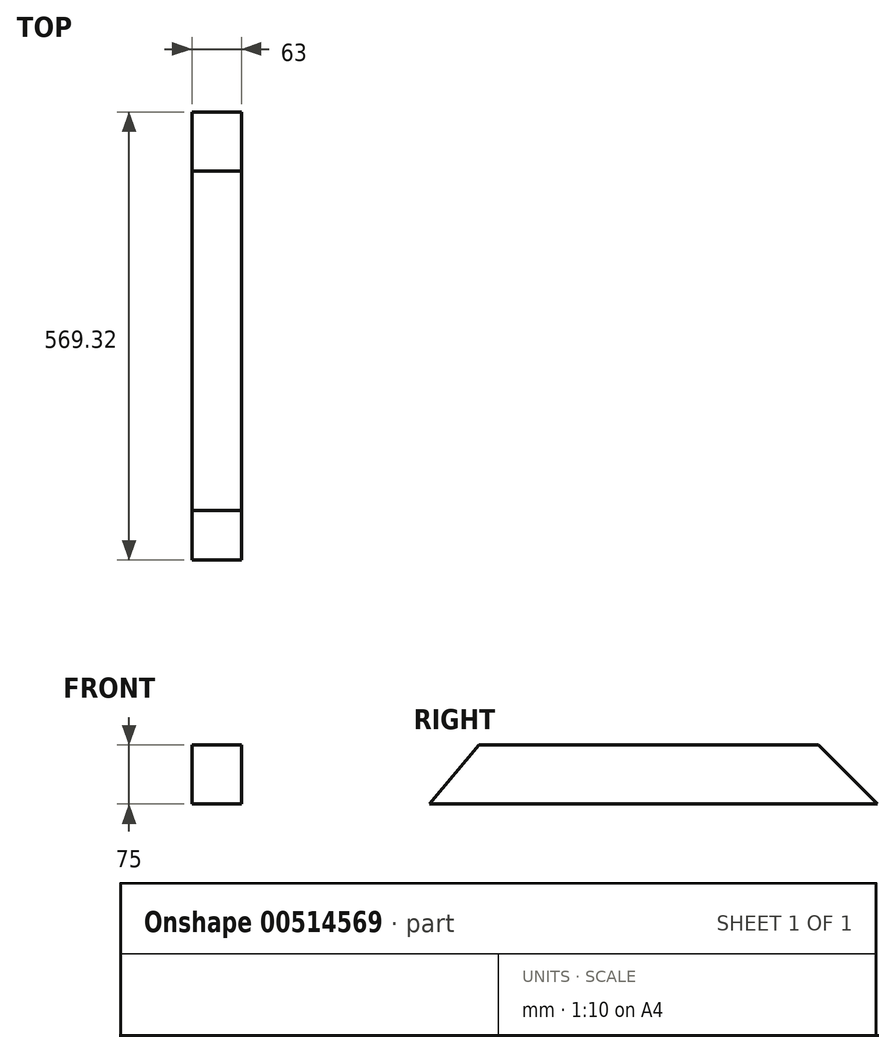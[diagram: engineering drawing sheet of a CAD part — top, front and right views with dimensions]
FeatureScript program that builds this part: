
annotation { "Feature Type Name" : "Feature", "Feature Type Description" : "" }
export const myFeature = defineFeature(function(context is Context, id is Id, definition is map)
    precondition{}
    {
        {
            var Q0;
            Q0=qCreatedBy(makeId("Front.planeOp"),FACE);
            var sketch = newSketch(context, id + "F0", { "sketchPlane" : qUnion([Q0])});
            skLineSegment(sketch, "E0.bottom", {"start": v(31.5, 37.5) * mm, "end": v(-31.5, 37.5) * mm});
            skLineSegment(sketch, "E0.top", {"start": v(31.5, -37.5) * mm, "end": v(-31.5, -37.5) * mm});
            skLineSegment(sketch, "E0.left", {"start": v(31.5, 37.5) * mm, "end": v(31.5, -37.5) * mm});
            skLineSegment(sketch, "E0.right", {"start": v(-31.5, 37.5) * mm, "end": v(-31.5, -37.5) * mm});
            skPoint(sketch, "E0.middle", {"position": v(0, 0) * mm});
            skSolve(sketch);
        }
        {
            var Q0;
            Q0=qSketchRegion(id+"F0",true);
            extrude(context, id + "F1", {"entities" : qUnion([Q0]), "depth" : 569.32 * mm});
        }
        {
            var Q0;
            Q0=makeQuery(id+"F1.opExtrude","SWEPT_FACE",FACE,{"disambiguationData":[OSD([sQuery(id+"F0.wireOp",EDGE,"E0.right")])]});
            var sketch = newSketch(context, id + "F2", { "sketchPlane" : qUnion([Q0])});
            skLineSegment(sketch, "E1", {"start": v(0, -37.5) * mm, "end": v(75, 37.5) * mm});
            skLineSegment(sketch, "E2", {"start": v(75, 37.5) * mm, "end": v(0, 37.5) * mm});
            skLineSegment(sketch, "E3", {"start": v(0, 37.5) * mm, "end": v(0, -37.5) * mm});
            skLineSegment(sketch, "E4", {"start": v(569.32, -37.5) * mm, "end": v(506.38, 37.5) * mm});
            skLineSegment(sketch, "E5", {"start": v(506.38, 37.5) * mm, "end": v(569.32, 37.5) * mm});
            skLineSegment(sketch, "E6", {"start": v(569.32, 37.5) * mm, "end": v(569.32, -37.5) * mm});
            skSolve(sketch);
        }
        {
            var Q0;
            Q0=qSketchRegion(id+"F2",true);
            extrude(context, id + "F3", {"entities" : qUnion([Q0]), "operationType" : NewBodyOperationType.REMOVE, "endBound" : BoundingType.THROUGH_ALL, "oppositeDirection" : true, "depth" : 25 * mm});
        }
    });
